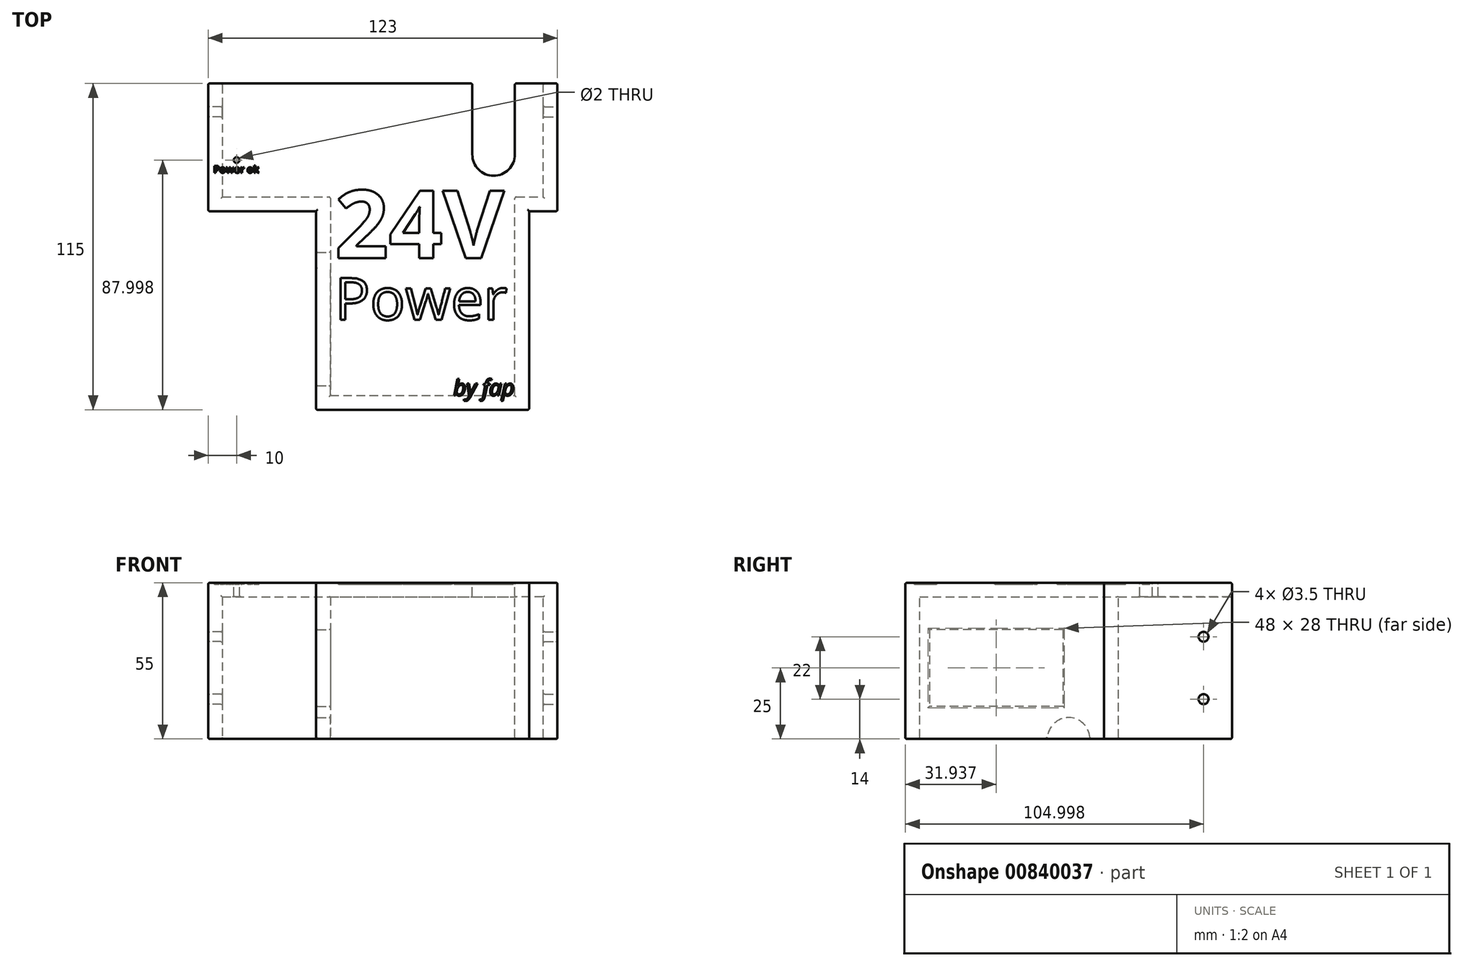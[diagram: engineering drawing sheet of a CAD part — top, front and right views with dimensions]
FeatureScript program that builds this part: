
annotation { "Feature Type Name" : "Feature", "Feature Type Description" : "" }
export const myFeature = defineFeature(function(context is Context, id is Id, definition is map)
    precondition{}
    {
        {
            var Q0;
            Q0=qCreatedBy(makeId("Top.planeOp"),FACE);
            var sketch = newSketch(context, id + "F0", { "sketchPlane" : qUnion([Q0])});
            skLineSegment(sketch, "E0", {"start": v(-61.5, 61.55) * mm, "end": v(-61.5, 16.55) * mm});
            skLineSegment(sketch, "E1", {"start": v(-61.5, 16.55) * mm, "end": v(-18.5, 16.55) * mm});
            skLineSegment(sketch, "E2", {"start": v(-18.5, 16.55) * mm, "end": v(-18.5, -48.45) * mm});
            skLineSegment(sketch, "E3", {"start": v(-18.5, -48.45) * mm, "end": v(46.5, -48.45) * mm});
            skLineSegment(sketch, "E4", {"start": v(46.5, -48.45) * mm, "end": v(46.5, 16.55) * mm});
            skLineSegment(sketch, "E5", {"start": v(46.5, 16.55) * mm, "end": v(61.5, 16.55) * mm});
            skLineSegment(sketch, "E6", {"start": v(61.5, 16.55) * mm, "end": v(61.5, 61.55) * mm});
            skLineSegment(sketch, "E7", {"start": v(61.5, 61.55) * mm, "end": v(46.5, 61.55) * mm});
            skArc(sketch, "E8.MirrorCS", {"start": v(46.5, 36.55) * mm, "mid": v(39, 29.05) * mm, "end": v(31.5, 36.55) * mm});
            skLineSegment(sketch, "E9.MirrorCS", {"start": v(31.5, 61.55) * mm, "end": v(31.5, 36.55) * mm});
            skLineSegment(sketch, "E10.MirrorCS", {"start": v(46.5, 61.55) * mm, "end": v(46.5, 36.55) * mm});
            skLineSegment(sketch, "E11", {"start": v(-61.5, 61.55) * mm, "end": v(31.5, 61.55) * mm});
            skLineSegment(sketch, "E12", {"start": v(31.5, 36.55) * mm, "end": v(46.5, 36.55) * mm, "construction": true});
            skCircle(sketch, "E13", {"center": v(-51.5, 34.55) * mm, "radius": 1 * mm});
            skLineSegment(sketch, "E14", {"start": v(-51.5, 43.05) * mm, "end": v(-51.5, 26.44) * mm, "construction": true});
            skSolve(sketch);
        }
        {
            var Q0;
            Q0=makeQuery(id+"F0.imprint","IMPRINT",FACE,{"disambiguationData":[TD([[makeQuery(id+"F0.imprint","IMPRINT",EDGE,{"derivedFrom":sQuery(id+"F0.wireOp",EDGE,"E0")}),1.0]])]});
            extrude(context, id + "F1", {"entities" : qUnion([Q0]), "oppositeDirection" : true, "depth" : 5 * mm, "offsetDistance" : 25 * mm});
        }
        {
            var Q0;
            Q0=makeQuery(id+"F1.opExtrude","SWEPT_FACE",FACE,{"disambiguationData":[OSD([sQuery(id+"F0.wireOp",EDGE,"E3")])]});
            var sketch = newSketch(context, id + "F2", { "sketchPlane" : qUnion([Q0])});
            skLineSegment(sketch, "E15", {"start": v(-18.5, 0) * mm, "end": v(-18.5, -55) * mm});
            skLineSegment(sketch, "E16", {"start": v(-18.5, -55) * mm, "end": v(46.5, -55) * mm});
            skLineSegment(sketch, "E17", {"start": v(46.5, -55) * mm, "end": v(46.5, 0) * mm});
            skSolve(sketch);
        }
        {
            var Q0;
            {var subQ2=sQuery(id+"F2.wireOp",EDGE,"E16");Q0=makeQuery(id+"F2.imprint","IMPRINT",FACE,{"disambiguationData":[TD([[makeQuery(id+"F2.imprint","IMPRINT",EDGE,{"derivedFrom":subQ2}),1.0]])]});}
            var Q1;
            {var subQ1=sQuery(id+"F0.wireOp",EDGE,"E3");var subQ2=makeQuery(id+"F1.opExtrude","CAP_EDGE",EDGE,{"disambiguationData":[OSD([subQ1])],"isStart":true});Q1=makeQuery(id+"F2.imprint","IMPRINT",FACE,{"disambiguationData":[TD([[makeQuery(id+"F2.imprint","IMPRINT",EDGE,{"derivedFrom":subQ2}),-1.0]])]});}
            extrude(context, id + "F3", {"entities" : qUnion([Q0, Q1]), "operationType" : NewBodyOperationType.ADD, "depth" : 5 * mm, "offsetDistance" : 25 * mm});
        }
        {
            var Q0;
            Q0=makeQuery(id+"F1.opExtrude","SWEPT_FACE",FACE,{"disambiguationData":[OSD([sQuery(id+"F0.wireOp",EDGE,"E1")])]});
            var sketch = newSketch(context, id + "F4", { "sketchPlane" : qUnion([Q0])});
            skLineSegment(sketch, "E18", {"start": v(-61.5, 0) * mm, "end": v(-61.5, -55) * mm});
            skLineSegment(sketch, "E19", {"start": v(-61.5, -55) * mm, "end": v(-18.5, -55) * mm});
            skLineSegment(sketch, "E20", {"start": v(-18.5, -55) * mm, "end": v(-18.5, 0) * mm});
            skSolve(sketch);
        }
        {
            var Q0;
            {var subQ2=sQuery(id+"F4.wireOp",EDGE,"E19");Q0=makeQuery(id+"F4.imprint","IMPRINT",FACE,{"disambiguationData":[TD([[makeQuery(id+"F4.imprint","IMPRINT",EDGE,{"derivedFrom":subQ2}),1.0]])]});}
            var Q1;
            {var subQ1=sQuery(id+"F0.wireOp",EDGE,"E1");var subQ2=makeQuery(id+"F1.opExtrude","CAP_EDGE",EDGE,{"disambiguationData":[OSD([subQ1])],"isStart":true});Q1=makeQuery(id+"F4.imprint","IMPRINT",FACE,{"disambiguationData":[TD([[makeQuery(id+"F4.imprint","IMPRINT",EDGE,{"derivedFrom":subQ2}),-1.0]])]});}
            extrude(context, id + "F5", {"entities" : qUnion([Q0, Q1]), "operationType" : NewBodyOperationType.ADD, "oppositeDirection" : true, "depth" : 5 * mm, "offsetDistance" : 25 * mm});
        }
        {
            var Q0;
            Q0=makeQuery(id+"F1.opExtrude","SWEPT_FACE",FACE,{"disambiguationData":[OSD([sQuery(id+"F0.wireOp",EDGE,"E5")])]});
            var sketch = newSketch(context, id + "F6", { "sketchPlane" : qUnion([Q0])});
            skLineSegment(sketch, "E21", {"start": v(61.5, 0) * mm, "end": v(61.5, -55) * mm});
            skLineSegment(sketch, "E22", {"start": v(61.5, -55) * mm, "end": v(46.5, -55) * mm});
            skLineSegment(sketch, "E23", {"start": v(46.5, -55) * mm, "end": v(46.5, 0) * mm});
            skSolve(sketch);
        }
        {
            var Q0;
            {var subQ1=sQuery(id+"F0.wireOp",EDGE,"E5");var subQ2=makeQuery(id+"F1.opExtrude","CAP_EDGE",EDGE,{"disambiguationData":[OSD([subQ1])],"isStart":true});Q0=makeQuery(id+"F6.imprint","IMPRINT",FACE,{"disambiguationData":[TD([[makeQuery(id+"F6.imprint","IMPRINT",EDGE,{"derivedFrom":subQ2}),-1.0]])]});}
            var Q1;
            {var subQ2=sQuery(id+"F6.wireOp",EDGE,"E22");Q1=makeQuery(id+"F6.imprint","IMPRINT",FACE,{"disambiguationData":[TD([[makeQuery(id+"F6.imprint","IMPRINT",EDGE,{"derivedFrom":subQ2}),-1.0]])]});}
            extrude(context, id + "F7", {"entities" : qUnion([Q0, Q1]), "operationType" : NewBodyOperationType.ADD, "oppositeDirection" : true, "depth" : 5 * mm, "offsetDistance" : 25 * mm});
        }
        {
            var Q0;
            Q0=makeQuery(id+"F5.boolean.opBoolean","MERGE",FACE,{"derivedFrom":[makeQuery(id+"F1.opExtrude","SWEPT_FACE",FACE,{"disambiguationData":[OSD([sQuery(id+"F0.wireOp",EDGE,"E0")])]}),makeQuery(id+"F5.opExtrude","SWEPT_FACE",FACE,{"disambiguationData":[OSD([sQuery(id+"F4.wireOp",EDGE,"E18")])]})]});
            var sketch = newSketch(context, id + "F8", { "sketchPlane" : qUnion([Q0])});
            skLineSegment(sketch, "E24", {"start": v(-61.55, 0) * mm, "end": v(-61.55, -55) * mm});
            skLineSegment(sketch, "E25", {"start": v(-61.55, -55) * mm, "end": v(-16.55, -55) * mm});
            skLineSegment(sketch, "E26", {"start": v(-51.55, 0) * mm, "end": v(-51.55, -55) * mm, "construction": true});
            skCircle(sketch, "E27", {"center": v(-51.55, -19) * mm, "radius": 1.75 * mm});
            skCircle(sketch, "E28", {"center": v(-51.55, -41) * mm, "radius": 1.75 * mm});
            skSolve(sketch);
        }
        {
            var Q0;
            {var subQ1=makeQuery(id+"F1.opExtrude","CAP_EDGE",EDGE,{"disambiguationData":[OSD([sQuery(id+"F0.wireOp",EDGE,"E0")])],"isStart":false});Q0=makeQuery(id+"F8.imprint","IMPRINT",FACE,{"disambiguationData":[TD([[makeQuery(id+"F8.imprint","IMPRINT",EDGE,{"derivedFrom":subQ1}),-1.0]])]});}
            var Q1;
            {var subQ0=sQuery(id+"F0.wireOp",EDGE,"E0");var subQ1=makeQuery(id+"F1.opExtrude","CAP_EDGE",EDGE,{"disambiguationData":[OSD([subQ0])],"isStart":true});Q1=makeQuery(id+"F8.imprint","IMPRINT",FACE,{"disambiguationData":[TD([[makeQuery(id+"F8.imprint","IMPRINT",EDGE,{"derivedFrom":subQ1}),-1.0]])]});}
            extrude(context, id + "F9", {"entities" : qUnion([Q0, Q1]), "operationType" : NewBodyOperationType.ADD, "oppositeDirection" : true, "depth" : 5 * mm, "offsetDistance" : 25 * mm});
        }
        {
            var Q0;
            Q0=makeQuery(id+"F3.boolean.opBoolean","MERGE",FACE,{"derivedFrom":[makeQuery(id+"F1.opExtrude","SWEPT_FACE",FACE,{"disambiguationData":[OSD([sQuery(id+"F0.wireOp",EDGE,"E2")])]}),makeQuery(id+"F3.opExtrude","SWEPT_FACE",FACE,{"disambiguationData":[OSD([sQuery(id+"F2.wireOp",EDGE,"E15")])]})]});
            var sketch = newSketch(context, id + "F10", { "sketchPlane" : qUnion([Q0])});
            skLineSegment(sketch, "E29", {"start": v(-16.55, 0) * mm, "end": v(-16.55, -55) * mm});
            skLineSegment(sketch, "E30", {"start": v(-16.55, -55) * mm, "end": v(-11.55, -55) * mm});
            skArc(sketch, "E31", {"start": v(3.45, -55) * mm, "mid": v(-4.05, -47.5) * mm, "end": v(-11.55, -55) * mm});
            skLineSegment(sketch, "E32.trimOffspring", {"start": v(3.45, -55) * mm, "end": v(53.45, -55) * mm});
            skLineSegment(sketch, "E33.bottom", {"start": v(-1.99, -16.5) * mm, "end": v(45.01, -16.5) * mm});
            skLineSegment(sketch, "E33.top", {"start": v(-1.99, -43.5) * mm, "end": v(45.01, -43.5) * mm});
            skLineSegment(sketch, "E33.left", {"start": v(-1.99, -16.5) * mm, "end": v(-1.99, -43.5) * mm});
            skLineSegment(sketch, "E33.right", {"start": v(45.01, -16.5) * mm, "end": v(45.01, -43.5) * mm});
            skLineSegment(sketch, "E34", {"start": v(-16.55, -30) * mm, "end": v(53.45, -30) * mm, "construction": true});
            skSolve(sketch);
        }
        {
            var Q0;
            {var subQ2=sQuery(id+"F0.wireOp",EDGE,"E2");var subQ3=makeQuery(id+"F1.opExtrude","CAP_EDGE",EDGE,{"disambiguationData":[OSD([subQ2])],"isStart":false});Q0=makeQuery(id+"F10.imprint","IMPRINT",FACE,{"disambiguationData":[TD([[makeQuery(id+"F10.imprint","IMPRINT",EDGE,{"derivedFrom":subQ3}),1.0]])]});}
            var Q1;
            {var subQ1=makeQuery(id+"F1.opExtrude","CAP_EDGE",EDGE,{"disambiguationData":[OSD([sQuery(id+"F0.wireOp",EDGE,"E2")])],"isStart":false});Q1=makeQuery(id+"F10.imprint","IMPRINT",FACE,{"disambiguationData":[TD([[makeQuery(id+"F10.imprint","IMPRINT",EDGE,{"derivedFrom":subQ1}),-1.0]])]});}
            extrude(context, id + "F11", {"entities" : qUnion([Q0, Q1]), "operationType" : NewBodyOperationType.ADD, "depth" : 5 * mm, "offsetDistance" : 25 * mm});
        }
        {
            var Q0;
            Q0=makeQuery(id+"F7.boolean.opBoolean","MERGE",FACE,{"derivedFrom":[makeQuery(id+"F1.opExtrude","SWEPT_FACE",FACE,{"disambiguationData":[OSD([sQuery(id+"F0.wireOp",EDGE,"E6")])]}),makeQuery(id+"F7.opExtrude","SWEPT_FACE",FACE,{"disambiguationData":[OSD([sQuery(id+"F6.wireOp",EDGE,"E21")])]})]});
            var sketch = newSketch(context, id + "F12", { "sketchPlane" : qUnion([Q0])});
            skLineSegment(sketch, "E35", {"start": v(16.55, -55) * mm, "end": v(61.55, -55) * mm});
            skLineSegment(sketch, "E36", {"start": v(61.55, -55) * mm, "end": v(61.55, 0) * mm});
            skLineSegment(sketch, "E37", {"start": v(51.55, -5) * mm, "end": v(51.55, -55) * mm, "construction": true});
            skCircle(sketch, "E38", {"center": v(51.55, -19) * mm, "radius": 1.75 * mm});
            skCircle(sketch, "E39", {"center": v(51.55, -41) * mm, "radius": 1.75 * mm});
            skSolve(sketch);
        }
        {
            var Q0;
            {var subQ4=makeQuery(id+"F1.opExtrude","CAP_EDGE",EDGE,{"disambiguationData":[OSD([sQuery(id+"F0.wireOp",EDGE,"E6")])],"isStart":false});Q0=makeQuery(id+"F12.imprint","IMPRINT",FACE,{"disambiguationData":[TD([[makeQuery(id+"F12.imprint","IMPRINT",EDGE,{"derivedFrom":subQ4}),-1.0]])]});}
            var Q1;
            {var subQ0=sQuery(id+"F0.wireOp",EDGE,"E6");var subQ1=makeQuery(id+"F1.opExtrude","CAP_EDGE",EDGE,{"disambiguationData":[OSD([subQ0])],"isStart":true});Q1=makeQuery(id+"F12.imprint","IMPRINT",FACE,{"disambiguationData":[TD([[makeQuery(id+"F12.imprint","IMPRINT",EDGE,{"derivedFrom":subQ1}),-1.0]])]});}
            extrude(context, id + "F13", {"entities" : qUnion([Q0, Q1]), "operationType" : NewBodyOperationType.ADD, "oppositeDirection" : true, "depth" : 5 * mm, "offsetDistance" : 25 * mm});
        }
        {
            var Q0;
            Q0=makeQuery(id+"F3.boolean.opBoolean","MERGE",FACE,{"derivedFrom":[makeQuery(id+"F1.opExtrude","SWEPT_FACE",FACE,{"disambiguationData":[OSD([sQuery(id+"F0.wireOp",EDGE,"E4")])]}),makeQuery(id+"F3.opExtrude","SWEPT_FACE",FACE,{"disambiguationData":[OSD([sQuery(id+"F2.wireOp",EDGE,"E17")])]})]});
            var sketch = newSketch(context, id + "F14", { "sketchPlane" : qUnion([Q0])});
            skLineSegment(sketch, "E40", {"start": v(-53.45, -55) * mm, "end": v(16.55, -55) * mm});
            skLineSegment(sketch, "E41", {"start": v(16.55, -55) * mm, "end": v(16.55, 0) * mm});
            skSolve(sketch);
        }
        {
            var Q0;
            {var subQ4=makeQuery(id+"F1.opExtrude","CAP_EDGE",EDGE,{"disambiguationData":[OSD([sQuery(id+"F0.wireOp",EDGE,"E4")])],"isStart":false});Q0=makeQuery(id+"F14.imprint","IMPRINT",FACE,{"disambiguationData":[TD([[makeQuery(id+"F14.imprint","IMPRINT",EDGE,{"derivedFrom":subQ4}),-1.0]])]});}
            var Q1;
            {var subQ2=sQuery(id+"F0.wireOp",EDGE,"E4");var subQ3=makeQuery(id+"F1.opExtrude","CAP_EDGE",EDGE,{"disambiguationData":[OSD([subQ2])],"isStart":false});Q1=makeQuery(id+"F14.imprint","IMPRINT",FACE,{"disambiguationData":[TD([[makeQuery(id+"F14.imprint","IMPRINT",EDGE,{"derivedFrom":subQ3}),1.0]])]});}
            extrude(context, id + "F15", {"entities" : qUnion([Q0, Q1]), "operationType" : NewBodyOperationType.ADD, "depth" : 5 * mm, "offsetDistance" : 25 * mm});
        }
        {
            var Q0;
            {var subQ0=sQuery(id+"F0.wireOp",EDGE,"E4");var subQ1=sQuery(id+"F0.wireOp",EDGE,"E3");var subQ2=sQuery(id+"F0.wireOp",EDGE,"E2");Q0=makeQuery(id+"F15.boolean.opBoolean","MERGE",FACE,{"derivedFrom":[makeQuery(id+"F11.boolean.opBoolean","MERGE",FACE,{"derivedFrom":[makeQuery(id+"F3.boolean.opBoolean","MERGE",FACE,{"derivedFrom":[makeQuery(id+"F1.opExtrude","CAP_FACE",FACE,{"disambiguationData":[OSD([sQuery(id+"F0.wireOp",EDGE,"E0"),sQuery(id+"F0.wireOp",EDGE,"E1"),subQ2,subQ1,subQ0,sQuery(id+"F0.wireOp",EDGE,"E5"),sQuery(id+"F0.wireOp",EDGE,"E6"),sQuery(id+"F0.wireOp",EDGE,"E7")])],"isStart":true}),makeQuery(id+"F3.opExtrude","SWEPT_FACE",FACE,{"disambiguationData":[OSD([subQ1])]})]}),makeQuery(id+"F11.opExtrude","SWEPT_FACE",FACE,{"disambiguationData":[OSD([subQ2,subQ1,sQuery(id+"F2.wireOp",EDGE,"E15")])]})]}),makeQuery(id+"F15.opExtrude","SWEPT_FACE",FACE,{"disambiguationData":[OSD([subQ1,subQ0,sQuery(id+"F2.wireOp",EDGE,"E17")])]})]});}
            var sketch = newSketch(context, id + "F16", { "sketchPlane" : qUnion([Q0])});
            skText(sketch, "E42", { "text": "24V", "fontName": "OpenSans-Bold.ttf"});
            skText(sketch, "E43", { "text": "by fap", "fontName": "OpenSans-Italic.ttf"});
            skLineSegment(sketch, "E44", {"start": v(14, -53.45) * mm, "end": v(14, 22.85) * mm, "construction": true});
            skText(sketch, "E45", { "text": "Power", "fontName": "OpenSans-Regular.ttf"});
            skText(sketch, "E46", { "text": "Power ok", "fontName": "OpenSans-Bold.ttf"});
            const initialGuessF16  = {"E42": [-0.01694, 0, 1, 0, 0.024], "E43": [0.02483, -0.04845, 1, 0, 0.00563], "E45": [-0.01694, -0.02176, 1, 0, 0.01483], "E46": [-0.05968, 0.03005, 1, 0, 0.0025]};
            skSetInitialGuess(sketch, initialGuessF16);
            skSolve(sketch);
        }
        {
            var Q0;
            Q0 = qSketchRegion(id + "F16", true);
            extrude(context, id + "F17", {"entities" : qUnion([Q0]), "operationType" : NewBodyOperationType.REMOVE, "oppositeDirection" : true, "depth" : 0.5 * mm, "offsetDistance" : 25 * mm});
        }
        {
            var Q0;
            {var subQ0=sQuery(id+"F0.wireOp",EDGE,"E3");Q0=makeQuery(id+"F15.boolean.opBoolean","MERGE",EDGE,{"derivedFrom":[makeQuery(id+"F11.boolean.opBoolean","MERGE",EDGE,{"derivedFrom":[makeQuery(id+"F3.opExtrude","CAP_EDGE",EDGE,{"disambiguationData":[OSD([subQ0])],"isStart":false}),makeQuery(id+"F11.opExtrude","SWEPT_EDGE",EDGE,{"disambiguationData":[OSD([sQuery(id+"F0.wireOp",EDGE,"E2"),subQ0,sQuery(id+"F2.wireOp",EDGE,"E15")])]})]}),makeQuery(id+"F15.opExtrude","SWEPT_EDGE",EDGE,{"disambiguationData":[OSD([subQ0,sQuery(id+"F0.wireOp",EDGE,"E4"),sQuery(id+"F2.wireOp",EDGE,"E17")])]})]});}
            var Q1;
            Q1=makeQuery(id+"F15.opExtrude","CAP_EDGE",EDGE,{"disambiguationData":[OSD([sQuery(id+"F0.wireOp",EDGE,"E3"),sQuery(id+"F0.wireOp",EDGE,"E4"),sQuery(id+"F2.wireOp",EDGE,"E17")])],"isStart":false});
            var Q2;
            Q2=makeQuery(id+"F1.opExtrude","CAP_EDGE",EDGE,{"disambiguationData":[OSD([sQuery(id+"F0.wireOp",EDGE,"E5")])],"isStart":true});
            var Q3;
            Q3=makeQuery(id+"F1.opExtrude","CAP_EDGE",EDGE,{"disambiguationData":[OSD([sQuery(id+"F0.wireOp",EDGE,"E6")])],"isStart":true});
            var Q4;
            Q4=makeQuery(id+"F7.boolean.opBoolean","MERGE",EDGE,{"derivedFrom":[makeQuery(id+"F1.opExtrude","SWEPT_EDGE",EDGE,{"disambiguationData":[OSD([sQuery(id+"F0.wireOp",EDGE,"E5"),sQuery(id+"F0.wireOp",EDGE,"E6")])]}),makeQuery(id+"F7.opExtrude","CAP_EDGE",EDGE,{"disambiguationData":[OSD([sQuery(id+"F6.wireOp",EDGE,"E21")])],"isStart":true})]});
            var Q5;
            Q5=makeQuery(id+"F15.opExtrude","CAP_EDGE",EDGE,{"disambiguationData":[OSD([sQuery(id+"F14.wireOp",EDGE,"E41")])],"isStart":false});
            var Q6;
            Q6=makeQuery(id+"F15.opExtrude","CAP_EDGE",EDGE,{"disambiguationData":[OSD([sQuery(id+"F2.wireOp",EDGE,"E17")])],"isStart":false});
            var Q7;
            Q7=makeQuery(id+"F15.opExtrude","CAP_EDGE",EDGE,{"disambiguationData":[OSD([sQuery(id+"F14.wireOp",EDGE,"E40")])],"isStart":false});
            var Q8;
            Q8=makeQuery(id+"F15.boolean.opBoolean","MERGE",EDGE,{"derivedFrom":[makeQuery(id+"F11.boolean.opBoolean","MERGE",EDGE,{"derivedFrom":[makeQuery(id+"F3.opExtrude","CAP_EDGE",EDGE,{"disambiguationData":[OSD([sQuery(id+"F2.wireOp",EDGE,"E16")])],"isStart":false}),makeQuery(id+"F11.opExtrude","SWEPT_EDGE",EDGE,{"disambiguationData":[OSD([sQuery(id+"F2.wireOp",EDGE,"E15"),sQuery(id+"F10.wireOp",EDGE,"E32.trimOffspring")])]})]}),makeQuery(id+"F15.opExtrude","SWEPT_EDGE",EDGE,{"disambiguationData":[OSD([sQuery(id+"F2.wireOp",EDGE,"E17"),sQuery(id+"F14.wireOp",EDGE,"E40")])]})]});
            var Q9;
            Q9=makeQuery(id+"F7.opExtrude","CAP_EDGE",EDGE,{"disambiguationData":[OSD([sQuery(id+"F6.wireOp",EDGE,"E22")])],"isStart":true});
            var Q10;
            Q10=makeQuery(id+"F13.boolean.opBoolean","MERGE",EDGE,{"derivedFrom":[makeQuery(id+"F7.opExtrude","SWEPT_EDGE",EDGE,{"disambiguationData":[OSD([sQuery(id+"F6.wireOp",EDGE,"E21"),sQuery(id+"F6.wireOp",EDGE,"E22")])]}),makeQuery(id+"F13.opExtrude","CAP_EDGE",EDGE,{"disambiguationData":[OSD([sQuery(id+"F12.wireOp",EDGE,"E35")])],"isStart":true})]});
            var Q11;
            Q11=makeQuery(id+"F13.opExtrude","CAP_EDGE",EDGE,{"disambiguationData":[OSD([sQuery(id+"F12.wireOp",EDGE,"E39")])],"isStart":true});
            var Q12;
            Q12=makeQuery(id+"F13.opExtrude","CAP_EDGE",EDGE,{"disambiguationData":[OSD([sQuery(id+"F12.wireOp",EDGE,"E38")])],"isStart":true});
            var Q13;
            Q13=makeQuery(id+"F13.boolean.opBoolean","MERGE",EDGE,{"derivedFrom":[makeQuery(id+"F1.opExtrude","SWEPT_EDGE",EDGE,{"disambiguationData":[OSD([sQuery(id+"F0.wireOp",EDGE,"E6"),sQuery(id+"F0.wireOp",EDGE,"E7")])]}),makeQuery(id+"F13.opExtrude","CAP_EDGE",EDGE,{"disambiguationData":[OSD([sQuery(id+"F12.wireOp",EDGE,"E36")])],"isStart":true})]});
            var Q14;
            Q14=makeQuery(id+"F1.opExtrude","CAP_EDGE",EDGE,{"disambiguationData":[OSD([sQuery(id+"F0.wireOp",EDGE,"E7")])],"isStart":true});
            var Q15;
            Q15=makeQuery(id+"F1.opExtrude","CAP_EDGE",EDGE,{"disambiguationData":[OSD([sQuery(id+"F0.wireOp",EDGE,"E10.MirrorCS")])],"isStart":true});
            var Q16;
            Q16=makeQuery(id+"F1.opExtrude","CAP_EDGE",EDGE,{"disambiguationData":[OSD([sQuery(id+"F0.wireOp",EDGE,"E8.MirrorCS")])],"isStart":true});
            var Q17;
            Q17=makeQuery(id+"F1.opExtrude","CAP_EDGE",EDGE,{"disambiguationData":[OSD([sQuery(id+"F0.wireOp",EDGE,"E9.MirrorCS")])],"isStart":true});
            var Q18;
            Q18=makeQuery(id+"F1.opExtrude","CAP_EDGE",EDGE,{"disambiguationData":[OSD([sQuery(id+"F0.wireOp",EDGE,"E11")])],"isStart":true});
            var Q19;
            Q19=makeQuery(id+"F1.opExtrude","CAP_EDGE",EDGE,{"disambiguationData":[OSD([sQuery(id+"F0.wireOp",EDGE,"E0")])],"isStart":true});
            var Q20;
            Q20=makeQuery(id+"F1.opExtrude","CAP_EDGE",EDGE,{"disambiguationData":[OSD([sQuery(id+"F0.wireOp",EDGE,"E1")])],"isStart":true});
            var Q21;
            Q21=makeQuery(id+"F11.opExtrude","CAP_EDGE",EDGE,{"disambiguationData":[OSD([sQuery(id+"F0.wireOp",EDGE,"E2"),sQuery(id+"F0.wireOp",EDGE,"E3"),sQuery(id+"F2.wireOp",EDGE,"E15")])],"isStart":false});
            var Q22;
            Q22=makeQuery(id+"F5.boolean.opBoolean","MERGE",EDGE,{"derivedFrom":[makeQuery(id+"F1.opExtrude","SWEPT_EDGE",EDGE,{"disambiguationData":[OSD([sQuery(id+"F0.wireOp",EDGE,"E0"),sQuery(id+"F0.wireOp",EDGE,"E1")])]}),makeQuery(id+"F5.opExtrude","CAP_EDGE",EDGE,{"disambiguationData":[OSD([sQuery(id+"F4.wireOp",EDGE,"E18")])],"isStart":true})]});
            var Q23;
            Q23=makeQuery(id+"F11.opExtrude","CAP_EDGE",EDGE,{"disambiguationData":[OSD([sQuery(id+"F2.wireOp",EDGE,"E15")])],"isStart":false});
            var Q24;
            Q24=makeQuery(id+"F11.opExtrude","CAP_EDGE",EDGE,{"disambiguationData":[OSD([sQuery(id+"F10.wireOp",EDGE,"E29")])],"isStart":false});
            var Q25;
            Q25=makeQuery(id+"F9.opExtrude","CAP_EDGE",EDGE,{"disambiguationData":[OSD([sQuery(id+"F8.wireOp",EDGE,"E27")])],"isStart":true});
            var Q26;
            Q26=makeQuery(id+"F9.opExtrude","CAP_EDGE",EDGE,{"disambiguationData":[OSD([sQuery(id+"F8.wireOp",EDGE,"E28")])],"isStart":true});
            var Q27;
            Q27=makeQuery(id+"F9.boolean.opBoolean","MERGE",EDGE,{"derivedFrom":[makeQuery(id+"F1.opExtrude","SWEPT_EDGE",EDGE,{"disambiguationData":[OSD([sQuery(id+"F0.wireOp",EDGE,"E0"),sQuery(id+"F0.wireOp",EDGE,"E11")])]}),makeQuery(id+"F9.opExtrude","CAP_EDGE",EDGE,{"disambiguationData":[OSD([sQuery(id+"F8.wireOp",EDGE,"E24")])],"isStart":true})]});
            var Q28;
            Q28=makeQuery(id+"F9.boolean.opBoolean","MERGE",EDGE,{"derivedFrom":[makeQuery(id+"F5.opExtrude","SWEPT_EDGE",EDGE,{"disambiguationData":[OSD([sQuery(id+"F4.wireOp",EDGE,"E18"),sQuery(id+"F4.wireOp",EDGE,"E19")])]}),makeQuery(id+"F9.opExtrude","CAP_EDGE",EDGE,{"disambiguationData":[OSD([sQuery(id+"F8.wireOp",EDGE,"E25")])],"isStart":true})]});
            var Q29;
            Q29=makeQuery(id+"F5.opExtrude","CAP_EDGE",EDGE,{"disambiguationData":[OSD([sQuery(id+"F4.wireOp",EDGE,"E19")])],"isStart":true});
            var Q30;
            Q30=makeQuery(id+"F11.opExtrude","CAP_EDGE",EDGE,{"disambiguationData":[OSD([sQuery(id+"F10.wireOp",EDGE,"E33.top")])],"isStart":false});
            var Q31;
            Q31=makeQuery(id+"F11.opExtrude","CAP_EDGE",EDGE,{"disambiguationData":[OSD([sQuery(id+"F10.wireOp",EDGE,"E33.left")])],"isStart":false});
            var Q32;
            Q32=makeQuery(id+"F11.opExtrude","CAP_EDGE",EDGE,{"disambiguationData":[OSD([sQuery(id+"F10.wireOp",EDGE,"E33.right")])],"isStart":false});
            var Q33;
            Q33=makeQuery(id+"F11.opExtrude","CAP_EDGE",EDGE,{"disambiguationData":[OSD([sQuery(id+"F10.wireOp",EDGE,"E33.bottom")])],"isStart":false});
            var Q34;
            Q34=makeQuery(id+"F11.opExtrude","CAP_EDGE",EDGE,{"disambiguationData":[OSD([sQuery(id+"F10.wireOp",EDGE,"E32.trimOffspring")])],"isStart":false});
            var Q35;
            Q35=makeQuery(id+"F11.opExtrude","CAP_EDGE",EDGE,{"disambiguationData":[OSD([sQuery(id+"F10.wireOp",EDGE,"E31")])],"isStart":false});
            var Q36;
            Q36=makeQuery(id+"F11.opExtrude","CAP_EDGE",EDGE,{"disambiguationData":[OSD([sQuery(id+"F10.wireOp",EDGE,"E30")])],"isStart":false});
            var Q37;
            Q37=makeQuery(id+"F11.opExtrude","CAP_EDGE",EDGE,{"disambiguationData":[OSD([sQuery(id+"F10.wireOp",EDGE,"E32.trimOffspring")])],"isStart":true});
            var Q38;
            Q38=makeQuery(id+"F11.opExtrude","CAP_EDGE",EDGE,{"disambiguationData":[OSD([sQuery(id+"F10.wireOp",EDGE,"E31")])],"isStart":true});
            var Q39;
            Q39=makeQuery(id+"F11.boolean.opBoolean","MERGE",EDGE,{"derivedFrom":[makeQuery(id+"F5.opExtrude","SWEPT_EDGE",EDGE,{"disambiguationData":[OSD([sQuery(id+"F4.wireOp",EDGE,"E19"),sQuery(id+"F4.wireOp",EDGE,"E20")])]}),makeQuery(id+"F11.opExtrude","CAP_EDGE",EDGE,{"disambiguationData":[OSD([sQuery(id+"F10.wireOp",EDGE,"E30")])],"isStart":true})]});
            var Q40;
            Q40=makeQuery(id+"F5.opExtrude","CAP_EDGE",EDGE,{"disambiguationData":[OSD([sQuery(id+"F4.wireOp",EDGE,"E19")])],"isStart":false});
            var Q41;
            Q41=makeQuery(id+"F9.opExtrude","CAP_EDGE",EDGE,{"disambiguationData":[OSD([sQuery(id+"F8.wireOp",EDGE,"E25")])],"isStart":false});
            var Q42;
            Q42=makeQuery(id+"F9.opExtrude","CAP_EDGE",EDGE,{"disambiguationData":[OSD([sQuery(id+"F8.wireOp",EDGE,"E24")])],"isStart":false});
            var Q43;
            Q43=makeQuery(id+"F1.opExtrude","CAP_EDGE",EDGE,{"disambiguationData":[OSD([sQuery(id+"F0.wireOp",EDGE,"E11")])],"isStart":false});
            var Q44;
            Q44=makeQuery(id+"F1.opExtrude","SWEPT_EDGE",EDGE,{"disambiguationData":[OSD([sQuery(id+"F0.wireOp",EDGE,"E7"),sQuery(id+"F0.wireOp",EDGE,"E10.MirrorCS")])]});
            var Q45;
            Q45=makeQuery(id+"F1.opExtrude","CAP_EDGE",EDGE,{"disambiguationData":[OSD([sQuery(id+"F0.wireOp",EDGE,"E10.MirrorCS")])],"isStart":false});
            var Q46;
            Q46=makeQuery(id+"F1.opExtrude","CAP_EDGE",EDGE,{"disambiguationData":[OSD([sQuery(id+"F0.wireOp",EDGE,"E8.MirrorCS")])],"isStart":false});
            var Q47;
            Q47=makeQuery(id+"F1.opExtrude","CAP_EDGE",EDGE,{"disambiguationData":[OSD([sQuery(id+"F0.wireOp",EDGE,"E9.MirrorCS")])],"isStart":false});
            var Q48;
            Q48=makeQuery(id+"F9.opExtrude","SWEPT_EDGE",EDGE,{"disambiguationData":[OSD([sQuery(id+"F8.wireOp",EDGE,"E24"),sQuery(id+"F8.wireOp",EDGE,"E25")])]});
            var Q49;
            Q49=makeQuery(id+"F13.opExtrude","SWEPT_EDGE",EDGE,{"disambiguationData":[OSD([sQuery(id+"F12.wireOp",EDGE,"E35"),sQuery(id+"F12.wireOp",EDGE,"E36")])]});
            var Q50;
            Q50=makeQuery(id+"F11.opExtrude","SWEPT_EDGE",EDGE,{"disambiguationData":[OSD([sQuery(id+"F10.wireOp",EDGE,"E31"),sQuery(id+"F10.wireOp",EDGE,"E32.trimOffspring")])]});
            var Q51;
            Q51=makeQuery(id+"F11.opExtrude","SWEPT_EDGE",EDGE,{"disambiguationData":[OSD([sQuery(id+"F10.wireOp",EDGE,"E30"),sQuery(id+"F10.wireOp",EDGE,"E31")])]});
            var Q52;
            Q52=makeQuery(id+"F11.opExtrude","CAP_EDGE",EDGE,{"disambiguationData":[OSD([sQuery(id+"F10.wireOp",EDGE,"E33.left")])],"isStart":true});
            var Q53;
            Q53=makeQuery(id+"F11.opExtrude","CAP_EDGE",EDGE,{"disambiguationData":[OSD([sQuery(id+"F10.wireOp",EDGE,"E33.bottom")])],"isStart":true});
            var Q54;
            Q54=makeQuery(id+"F11.opExtrude","CAP_EDGE",EDGE,{"disambiguationData":[OSD([sQuery(id+"F10.wireOp",EDGE,"E33.top")])],"isStart":true});
            var Q55;
            Q55=makeQuery(id+"F11.opExtrude","CAP_EDGE",EDGE,{"disambiguationData":[OSD([sQuery(id+"F10.wireOp",EDGE,"E33.right")])],"isStart":true});
            var Q56;
            Q56=makeQuery(id+"F13.opExtrude","CAP_EDGE",EDGE,{"disambiguationData":[OSD([sQuery(id+"F12.wireOp",EDGE,"E39")])],"isStart":false});
            var Q57;
            Q57=makeQuery(id+"F13.opExtrude","CAP_EDGE",EDGE,{"disambiguationData":[OSD([sQuery(id+"F12.wireOp",EDGE,"E38")])],"isStart":false});
            var Q58;
            Q58=makeQuery(id+"F13.opExtrude","CAP_EDGE",EDGE,{"disambiguationData":[OSD([sQuery(id+"F12.wireOp",EDGE,"E35")])],"isStart":false});
            var Q59;
            Q59=makeQuery(id+"F7.opExtrude","CAP_EDGE",EDGE,{"disambiguationData":[OSD([sQuery(id+"F6.wireOp",EDGE,"E22")])],"isStart":false});
            var Q60;
            Q60=makeQuery(id+"F15.boolean.opBoolean","MERGE",EDGE,{"derivedFrom":[makeQuery(id+"F7.opExtrude","SWEPT_EDGE",EDGE,{"disambiguationData":[OSD([sQuery(id+"F6.wireOp",EDGE,"E22"),sQuery(id+"F6.wireOp",EDGE,"E23")])]}),makeQuery(id+"F15.opExtrude","CAP_EDGE",EDGE,{"disambiguationData":[OSD([sQuery(id+"F14.wireOp",EDGE,"E40")])],"isStart":true})]});
            var Q61;
            Q61=makeQuery(id+"F3.opExtrude","CAP_EDGE",EDGE,{"disambiguationData":[OSD([sQuery(id+"F2.wireOp",EDGE,"E16")])],"isStart":true});
            var Q62;
            Q62=makeQuery(id+"F9.opExtrude","CAP_EDGE",EDGE,{"disambiguationData":[OSD([sQuery(id+"F8.wireOp",EDGE,"E28")])],"isStart":false});
            var Q63;
            Q63=makeQuery(id+"F9.opExtrude","CAP_EDGE",EDGE,{"disambiguationData":[OSD([sQuery(id+"F8.wireOp",EDGE,"E27")])],"isStart":false});
            var Q64;
            Q64=makeQuery(id+"F1.opExtrude","CAP_EDGE",EDGE,{"disambiguationData":[OSD([sQuery(id+"F0.wireOp",EDGE,"E13")])],"isStart":false});
            var Q65;
            Q65=makeQuery(id+"F5.opExtrude","CAP_EDGE",EDGE,{"disambiguationData":[OSD([sQuery(id+"F4.wireOp",EDGE,"E20")])],"isStart":false});
            var Q66;
            Q66=makeQuery(id+"F1.opExtrude","CAP_EDGE",EDGE,{"disambiguationData":[OSD([sQuery(id+"F0.wireOp",EDGE,"E13")])],"isStart":true});
            var Q67;
            Q67=makeQuery(id+"F7.opExtrude","CAP_EDGE",EDGE,{"disambiguationData":[OSD([sQuery(id+"F6.wireOp",EDGE,"E23")])],"isStart":false});
            var Q68;
            Q68=makeQuery(id+"F1.opExtrude","SWEPT_EDGE",EDGE,{"disambiguationData":[OSD([sQuery(id+"F0.wireOp",EDGE,"E9.MirrorCS"),sQuery(id+"F0.wireOp",EDGE,"E11")])]});
            var Q69;
            Q69=makeQuery(id+"F13.opExtrude","CAP_EDGE",EDGE,{"disambiguationData":[OSD([sQuery(id+"F12.wireOp",EDGE,"E36")])],"isStart":false});
            var Q70;
            Q70=makeQuery(id+"F1.opExtrude","CAP_EDGE",EDGE,{"disambiguationData":[OSD([sQuery(id+"F0.wireOp",EDGE,"E7")])],"isStart":false});
            fillet(context, id + "F18", {"entities" : qUnion([Q0, Q1, Q2, Q3, Q4, Q5, Q6, Q7, Q8, Q9, Q10, Q11, Q12, Q13, Q14, Q15, Q16, Q17, Q18, Q19, Q20, Q21, Q22, Q23, Q24, Q25, Q26, Q27, Q28, Q29, Q30, Q31, Q32, Q33, Q34, Q35, Q36, Q37, Q38, Q39, Q40, Q41, Q42, Q43, Q44, Q45, Q46, Q47, Q48, Q49, Q50, Q51, Q52, Q53, Q54, Q55, Q56, Q57, Q58, Q59, Q60, Q61, Q62, Q63, Q64, Q65, Q66, Q67, Q68, Q69, Q70]), "radius" : 0.5 * mm, "tangentPropagation" : true, "allowEdgeOverflow" : false});
        }
    });
